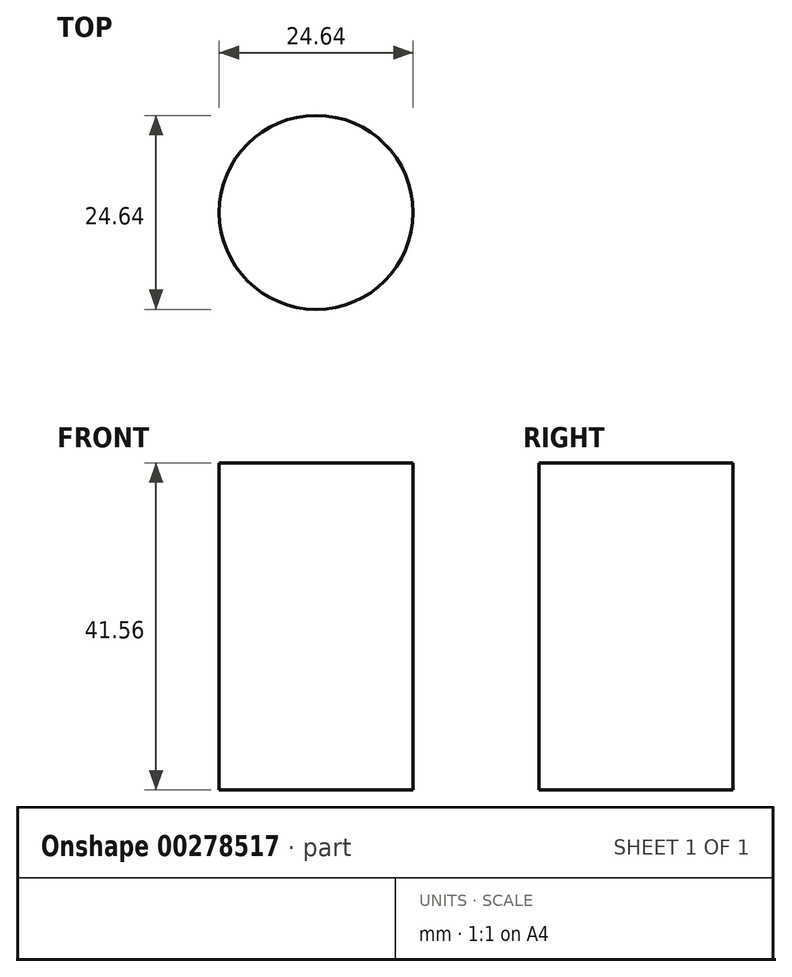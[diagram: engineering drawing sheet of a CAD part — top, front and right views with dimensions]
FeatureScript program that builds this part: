
annotation { "Feature Type Name" : "Feature", "Feature Type Description" : "" }
export const myFeature = defineFeature(function(context is Context, id is Id, definition is map)
    precondition{}
    {
        {
            var Q0;
            Q0=qCreatedBy(makeId("Right.planeOp"),FACE);
            var sketch = newSketch(context, id + "F0", { "sketchPlane" : qUnion([Q0])});
            skLineSegment(sketch, "E0", {"start": v(0, 0) * mm, "end": v(0, -41.56) * mm});
            skSolve(sketch);
        }
        {
            var Q0;
            Q0=qCreatedBy(makeId("Top.planeOp"),FACE);
            var sketch = newSketch(context, id + "F1", { "sketchPlane" : qUnion([Q0])});
            skCircle(sketch, "E1", {"center": v(0, 0) * mm, "radius": 12.32 * mm});
            skSolve(sketch);
        }
        {
            var Q0;
            Q0=makeQuery(id+"F1.imprint","IMPRINT",FACE,{"disambiguationData":[TD([[makeQuery(id+"F1.imprint","IMPRINT",EDGE,{"derivedFrom":sQuery(id+"F1.wireOp",EDGE,"E1")}),1.0]])]});
            var Q1;
            Q1=sQuery(id+"F0.wireOp",EDGE,"E0");
            sweep(context, id + "F2", {"profiles" : qUnion([Q0]), "path" : qUnion([Q1])});
        }
    });
